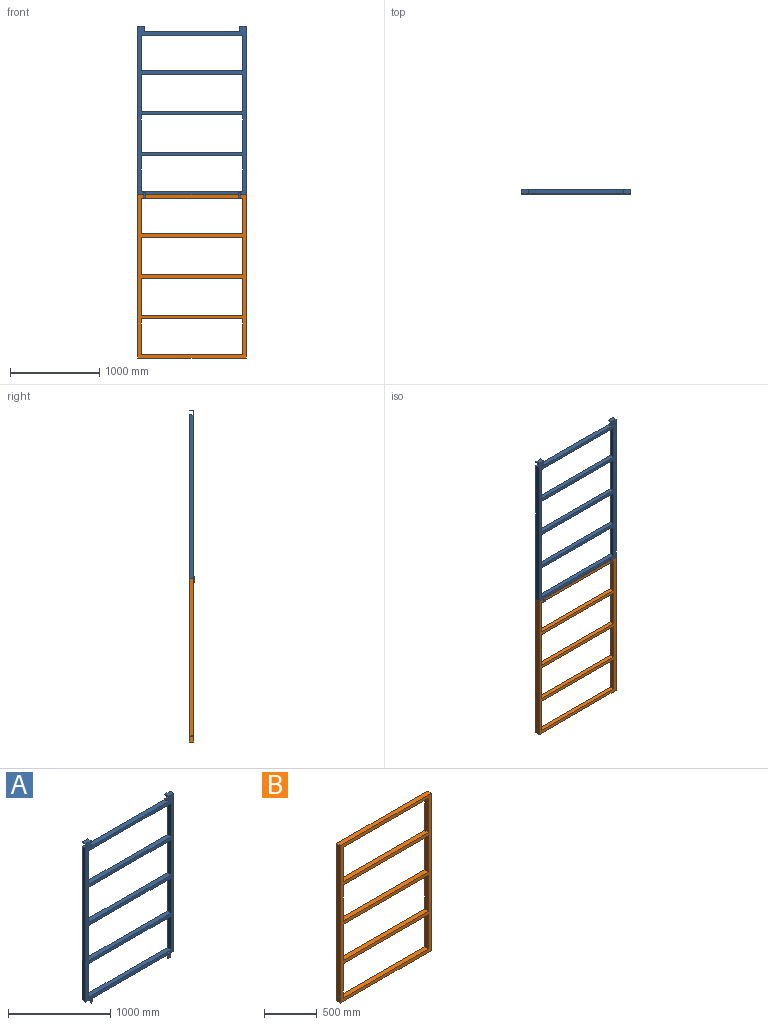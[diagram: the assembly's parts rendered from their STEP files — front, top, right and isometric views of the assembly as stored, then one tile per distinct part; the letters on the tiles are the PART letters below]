
ASSEMBLY  parts=2 mates=1
PART A: 46 faces, bbox 1219.2x60.3x1930.4 mm
  f0: plane 1892.3x1219.2mm, normal (0,-1,0), area 365483.1mm2, adj f2,f3,f5,f6,f7,f8,f9,f10
  f1: plane 76.2x9.53mm, normal (0,1,0), area 725.8mm2, adj f2,f3,f30,f31
  f2: plane 1892.3x50.8mm, normal (-1,0,0), area 94153mm2, adj f0,f1,f4,f20,f30,f31,f32,f33
  f3: plane 63.5x50.8mm, normal (1,0,0), area 1250mm2, adj f0,f1,f4,f5,f30,f31,f32,f33
  f4: plane 1838.33x1219.2mm, normal (0,1,0), area 358547.7mm2, adj f2,f3,f5,f6,f7,f8,f9,f10
  f5: plane 1066.8x50.8mm, normal (0,0,1), area 54193.4mm2, adj f0,f3,f4,f25
  f6: plane 419.1x50.8mm, normal (1,0,0), area 21290.3mm2, adj f0,f4,f7,f23
  f7: plane 1143x50.8mm, normal (0,0,-1), area 58064.4mm2, adj f0,f4,f6,f8
  f8: plane 419.1x50.8mm, normal (-1,0,0), area 21290.3mm2, adj f0,f4,f7,f23
  f9: plane 400.05x50.8mm, normal (1,0,0), area 20322.5mm2, adj f0,f4,f10,f19
  f10: plane 1143x50.8mm, normal (0,0,-1), area 58064.4mm2, adj f0,f4,f9,f11
  f11: plane 400.05x50.8mm, normal (-1,0,0), area 20322.5mm2, adj f0,f4,f10,f19
  f12: plane 1892.3x50.8mm, normal (1,0,0), area 94153mm2, adj f0,f4,f20,f24,f26,f27,f28,f29
  f13: plane 1143x50.8mm, normal (0,0,1), area 58064.4mm2, adj f0,f4,f14,f21
  f14: plane 400.05x50.8mm, normal (1,0,0), area 20322.5mm2, adj f0,f4,f13,f15
  f15: plane 1143x50.8mm, normal (0,0,-1), area 58064.4mm2, adj f0,f4,f14,f21
  f16: plane 1143x50.8mm, normal (0,0,1), area 58064.4mm2, adj f0,f4,f17,f22
  f17: plane 419.1x50.8mm, normal (1,0,0), area 21290.3mm2, adj f0,f4,f16,f18
  f18: plane 1143x50.8mm, normal (0,0,-1), area 58064.4mm2, adj f0,f4,f17,f22
  f19: plane 1143x50.8mm, normal (0,0,1), area 58064.4mm2, adj f0,f4,f9,f11
  f20: plane 1219.2x50.8mm, normal (0,0,-1), area 61935.4mm2, adj f0,f2,f4,f12,f39,f45
  f21: plane 400.05x50.8mm, normal (-1,0,0), area 20322.5mm2, adj f0,f4,f13,f15
  f22: plane 419.1x50.8mm, normal (-1,0,0), area 21290.3mm2, adj f0,f4,f16,f18
  f23: plane 1143x50.8mm, normal (0,0,1), area 58064.4mm2, adj f0,f4,f6,f8
  f24: plane 76.2x9.53mm, normal (0,1,0), area 725.8mm2, adj f12,f25,f26,f28
  f25: plane 63.5x50.8mm, normal (-1,0,0), area 1250mm2, adj f0,f4,f5,f24,f26,f27,f28,f29
  f26: plane 76.2x50.8mm, normal (0,0,1), area 3871mm2, adj f0,f12,f24,f25
  f27: plane 76.2x44.45mm, normal (0,0,1), area 3387.1mm2, adj f4,f12,f25,f29
  f28: plane 76.2x44.45mm, normal (0,0,-1), area 3387.1mm2, adj f12,f24,f25,f29
  f29: plane 76.2x44.45mm, normal (0,1,0), area 3387.1mm2, adj f12,f25,f27,f28
  f30: plane 76.2x50.8mm, normal (0,0,1), area 3871mm2, adj f0,f1,f2,f3
  f31: plane 76.2x44.45mm, normal (0,0,-1), area 3387.1mm2, adj f1,f2,f3,f33
  f32: plane 76.2x44.45mm, normal (0,0,1), area 3387.1mm2, adj f2,f3,f4,f33
  f33: plane 76.2x44.45mm, normal (0,1,0), area 3387.1mm2, adj f2,f3,f31,f32
  f34: plane 63.5x9.53mm, normal (1,0,0), area 604.8mm2, adj f0,f35,f37,f38,f39
  f35: plane 25.4x9.53mm, normal (0,0,1), area 241.9mm2, adj f0,f34,f36,f38
  f36: plane 63.5x9.53mm, normal (-1,0,0), area 604.8mm2, adj f0,f35,f37,f38,f39
  f37: plane 25.4x9.53mm, normal (0,0,-1), area 241.9mm2, adj f34,f36,f38,f39
  f38: plane 63.5x25.4mm, normal (0,-1,0), area 1612.9mm2, adj f34,f35,f36,f37
  f39: plane 38.1x25.4mm, normal (0,1,0), area 967.7mm2, adj f20,f34,f36,f37
  f40: plane 63.5x9.53mm, normal (-1,0,0), area 604.8mm2, adj f0,f41,f43,f44,f45
  f41: plane 25.4x9.53mm, normal (0,0,-1), area 241.9mm2, adj f40,f42,f44,f45
  f42: plane 63.5x9.53mm, normal (1,0,0), area 604.8mm2, adj f0,f41,f43,f44,f45
  f43: plane 25.4x9.53mm, normal (0,0,1), area 241.9mm2, adj f0,f40,f42,f44
  f44: plane 63.5x25.4mm, normal (0,-1,0), area 1612.9mm2, adj f40,f41,f42,f43
  f45: plane 38.1x25.4mm, normal (0,1,0), area 967.7mm2, adj f20,f40,f41,f42
PART B: 25 faces, bbox 1219.2x50.8x1828.8 mm
  f0: plane 400.05x50.8mm, normal (1,0,0), area 20163.6mm2, adj f1,f19,f20,f21,f23
  f1: plane 1143x50.8mm, normal (0,0,-1), area 58064.4mm2, adj f0,f2,f20,f21
  f2: plane 400.05x50.8mm, normal (-1,0,0), area 20322.5mm2, adj f1,f19,f20,f21
  f3: plane 1828.8x50.8mm, normal (1,0,0), area 92903mm2, adj f4,f15,f20,f21
  f4: plane 1219.2x50.8mm, normal (0,0,1), area 61935.4mm2, adj f3,f5,f20,f21
  f5: plane 1828.8x50.8mm, normal (-1,0,0), area 92744.1mm2, adj f4,f15,f20,f21,f24
  f6: plane 1143x50.8mm, normal (0,0,1), area 58064.4mm2, adj f7,f16,f20,f21
  f7: plane 400.05x50.8mm, normal (1,0,0), area 20322.5mm2, adj f6,f8,f20,f21
  f8: plane 1143x50.8mm, normal (0,0,-1), area 58064.4mm2, adj f7,f16,f20,f21
  f9: plane 1143x50.8mm, normal (0,0,1), area 58064.4mm2, adj f10,f17,f20,f21
  f10: plane 419.1x50.8mm, normal (1,0,0), area 21290.3mm2, adj f9,f11,f20,f21
  f11: plane 1143x50.8mm, normal (0,0,-1), area 58064.4mm2, adj f10,f17,f20,f21
  f12: plane 1143x50.8mm, normal (0,0,1), area 58064.4mm2, adj f13,f18,f20,f21
  f13: plane 419.1x50.8mm, normal (1,0,0), area 21290.3mm2, adj f12,f14,f20,f21
  f14: plane 1143x50.8mm, normal (0,0,-1), area 58064.4mm2, adj f13,f18,f20,f21
  f15: plane 1219.2x50.8mm, normal (0,0,-1), area 61935.4mm2, adj f3,f5,f20,f21
  f16: plane 400.05x50.8mm, normal (-1,0,0), area 20322.5mm2, adj f6,f8,f20,f21
  f17: plane 419.1x50.8mm, normal (-1,0,0), area 21290.3mm2, adj f9,f11,f20,f21
  f18: plane 419.1x50.8mm, normal (-1,0,0), area 21290.3mm2, adj f12,f14,f20,f21
  f19: plane 1143x50.8mm, normal (0,0,1), area 58064.4mm2, adj f0,f2,f20,f21
  f20: plane 1828.8x1219.2mm, normal (0,-1,0), area 357096.1mm2, adj f0,f1,f2,f3,f4,f5,f6,f7
  f21: plane 1828.8x1219.2mm, normal (0,1,0), area 357096.1mm2, adj f0,f1,f2,f3,f4,f5,f6,f7
  f22: cylinder r=6.35mm len=36.58mm, axis (-1,0,0), area 1459.3mm2, adj f23,f24
  f23: cone r=7.11mm half-angle=45deg, axis (1,0,0), area 45.6mm2, adj f0,f22
  f24: cone r=6.35mm half-angle=45deg, axis (-1,0,0), area 45.6mm2, adj f5,f22
PLACE A t=(253.5,233.57,110.98)mm
PLACE B t=(253.5,233.57,-1717.82)mm
MATE fastened B.f4 <-> A.f20  axis (0,0,1) through (253.5,233.57,-803.42)mm
